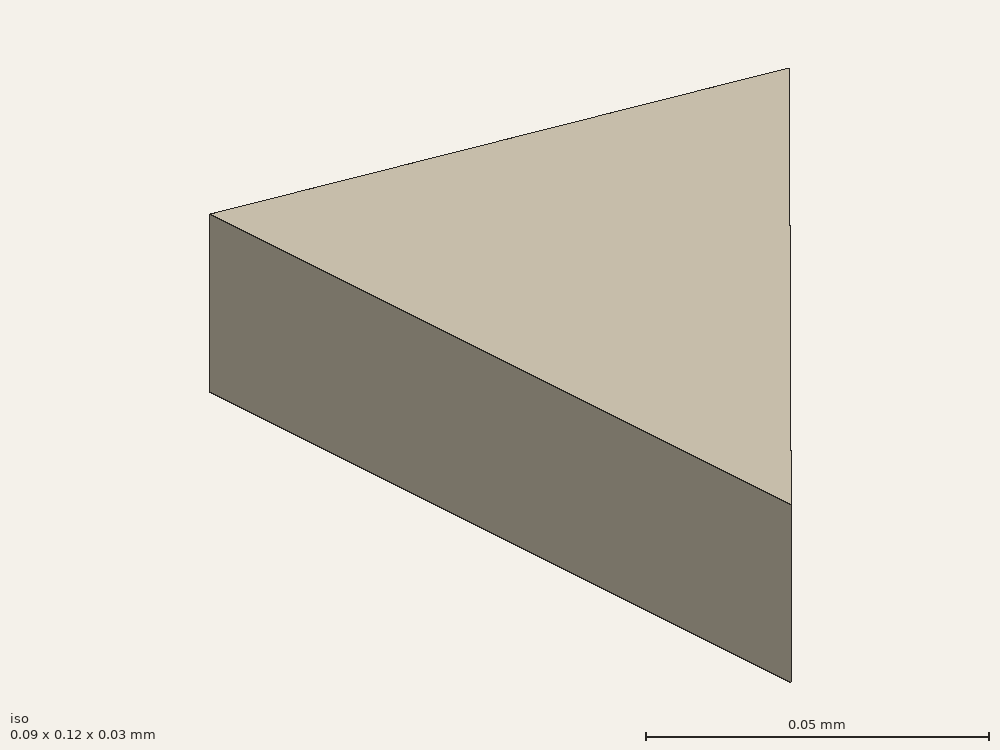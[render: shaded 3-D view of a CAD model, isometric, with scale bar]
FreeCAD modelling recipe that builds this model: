
FCSTD DOCUMENT  (FreeCAD 0.15R4671 (Git))
Label: triangle3
License: All rights reserved
LicenseURL: http://en.wikipedia.org/wiki/All_rights_reserved
objects: Sketcher::SketchObject×1, PartDesign::Pad×1
note: 3 computed .brp shape members not serialized (recipe doc carries the construction recipe); baked Part::Feature solids carry a one-line shape summary decoded from their .brp

FEATURE [Sketcher::SketchObject] Sketch
  sketch-geometry (3):
    g0: LineSegment StartX=-0.03 StartY=0.0498605 StartZ=0 EndX=-0.03 EndY=-0.0701395 EndZ=0
    g1: LineSegment StartX=-0.03 StartY=-0.0701395 StartZ=0 EndX=0.06 EndY=0.020279 EndZ=0
    g2: LineSegment StartX=0.06 StartY=0.020279 StartZ=0 EndX=-0.03 EndY=0.0498605 EndZ=0
  constraints (9):
    c: Coincident(g0,g1)
    c: Coincident(g1,g2)
    c: Coincident(g0,g2)
    c: Distance(g1,g0) = 0.09
    c: Distance(g-1,g2) = 0.038
    c: Distance(g-1,g0) = 0.03
    c: Distance(g0) = 0.12
    c: Parallel(g0,g-2)
    c: Distance(g0,g2) = 0.114
FEATURE [PartDesign::Pad] Pad
  Length = 0.03
  Length2 = 100
  Midplane = true
  Sketch = -> Sketch
  Type = 0
